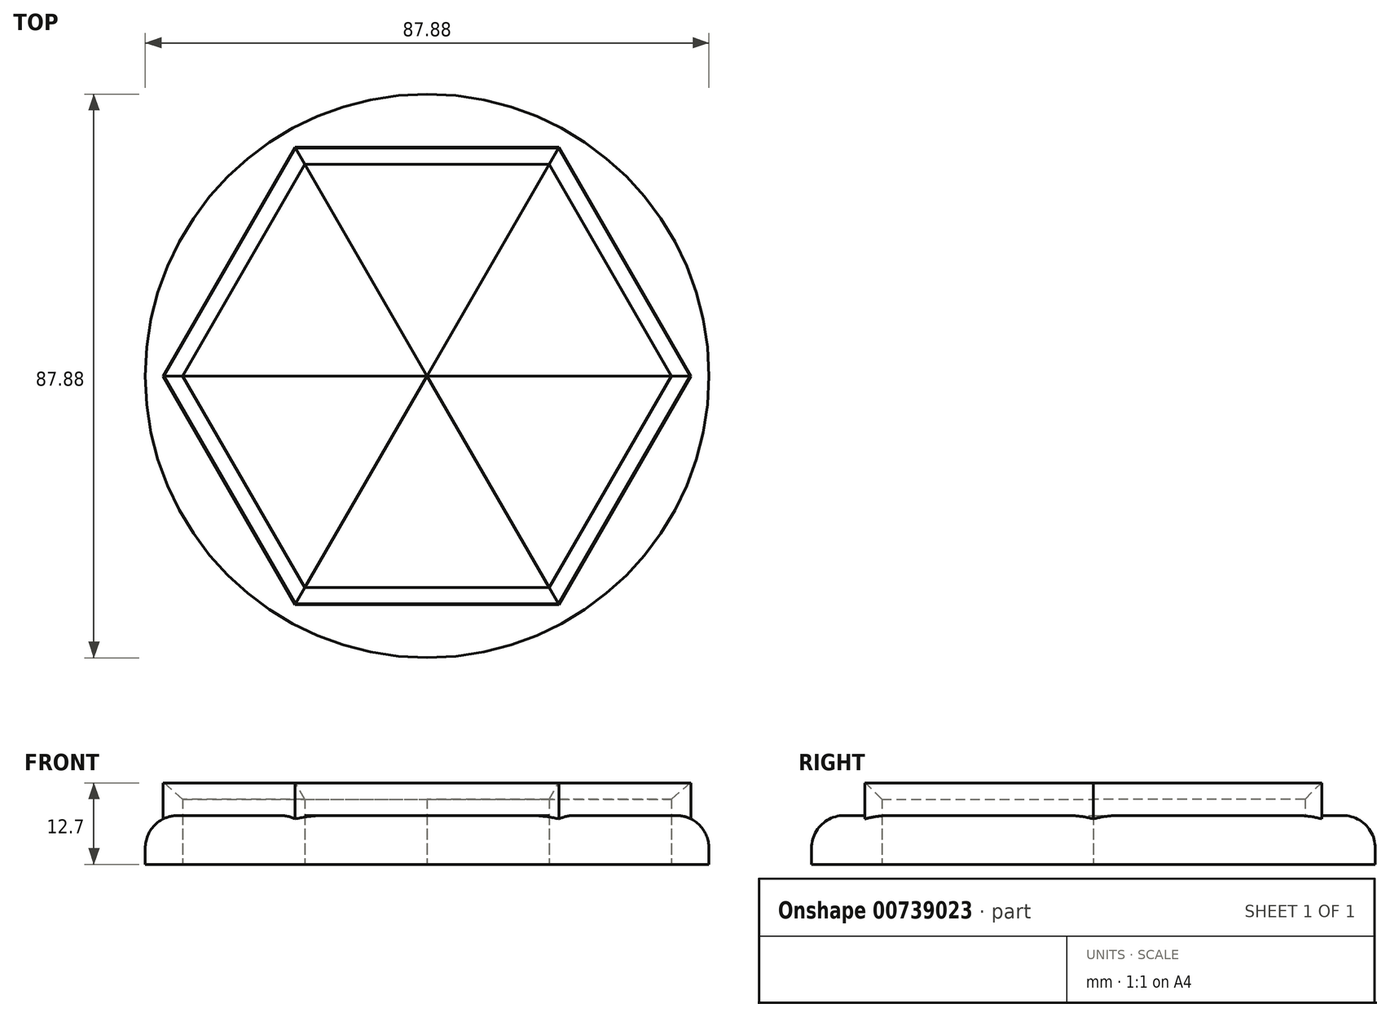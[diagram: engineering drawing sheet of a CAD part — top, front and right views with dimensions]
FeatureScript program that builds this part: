
annotation { "Feature Type Name" : "Feature", "Feature Type Description" : "" }
export const myFeature = defineFeature(function(context is Context, id is Id, definition is map)
    precondition{}
    {
        {
            var Q0;
            Q0=qCreatedBy(makeId("Top.planeOp"),FACE);
            var sketch = newSketch(context, id + "F0", { "sketchPlane" : qUnion([Q0])});
            skLineSegment(sketch, "E0.0", {"start": v(19.05, -33) * mm, "end": v(-19.05, -33) * mm});
            skLineSegment(sketch, "E0.1", {"start": v(-19.05, -33) * mm, "end": v(-38.1, 0) * mm});
            skLineSegment(sketch, "E0.2", {"start": v(-38.1, 0) * mm, "end": v(-19.05, 33) * mm});
            skLineSegment(sketch, "E0.3", {"start": v(-19.05, 33) * mm, "end": v(19.05, 33) * mm});
            skLineSegment(sketch, "E0.4", {"start": v(19.05, 33) * mm, "end": v(38.1, 0) * mm});
            skLineSegment(sketch, "E0.5", {"start": v(38.1, 0) * mm, "end": v(19.05, -33) * mm});
            skCircle(sketch, "E1", {"center": v(0, 0) * mm, "radius": 43.94 * mm});
            skLineSegment(sketch, "E2", {"start": v(-38.1, 0) * mm, "end": v(-43.94, 0) * mm});
            skLineSegment(sketch, "E3", {"start": v(-19.05, -33) * mm, "end": v(19.05, 33) * mm});
            skLineSegment(sketch, "E4", {"start": v(19.05, -33) * mm, "end": v(-19.05, 33) * mm});
            skLineSegment(sketch, "E5", {"start": v(-38.1, 0) * mm, "end": v(38.1, 0) * mm});
            skCircle(sketch, "E6", {"center": v(0, 0) * mm, "radius": 38.1 * mm, "construction": true});
            skCircle(sketch, "E7", {"center": v(0, 0) * mm, "radius": 41.15 * mm});
            skLineSegment(sketch, "E8", {"start": v(0, 38.1) * mm, "end": v(0, 41.15) * mm});
            skPoint(sketch, "E8.startSnap0", {"position": v(0, 33) * mm});
            skCircle(sketch, "E9.cCircle", {"center": v(0, 0) * mm, "radius": 41.15 * mm, "construction": true});
            skLineSegment(sketch, "E9.0", {"start": v(41.15, 0) * mm, "end": v(20.57, -35.64) * mm});
            skLineSegment(sketch, "E9.1", {"start": v(20.57, -35.64) * mm, "end": v(-20.57, -35.64) * mm});
            skLineSegment(sketch, "E9.2", {"start": v(-20.57, -35.64) * mm, "end": v(-41.15, 0) * mm});
            skLineSegment(sketch, "E9.3", {"start": v(-41.15, 0) * mm, "end": v(-20.57, 35.64) * mm});
            skLineSegment(sketch, "E9.4", {"start": v(-20.57, 35.64) * mm, "end": v(20.57, 35.64) * mm});
            skLineSegment(sketch, "E9.5", {"start": v(20.57, 35.64) * mm, "end": v(41.15, 0) * mm});
            skSolve(sketch);
        }
        {
            var Q0;
            Q0=makeQuery(id+"F0.imprint","IMPRINT",FACE,{"disambiguationData":[TD([[makeQuery(id+"F0.imprint","IMPRINT",EDGE,{"derivedFrom":sQuery(id+"F0.wireOp",EDGE,"E0.0")}),1.0]])]});
            extrude(context, id + "F1", {"entities" : qUnion([Q0]), "depth" : 12.7 * mm, "offsetDistance" : 25.4 * mm});
        }
        {
            var Q0;
            {var subQ0=sQuery(id+"F0.wireOp",EDGE,"E0.3");Q0=makeQuery(id+"F0.imprint","IMPRINT",FACE,{"disambiguationData":[TD([[makeQuery(id+"F0.imprint","IMPRINT",EDGE,{"derivedFrom":subQ0}),-1.0]])]});}
            extrude(context, id + "F2", {"entities" : qUnion([Q0]), "operationType" : NewBodyOperationType.ADD, "depth" : 10.16 * mm, "offsetDistance" : 25.4 * mm});
        }
        {
            var Q0;
            {var subQ0=sQuery(id+"F0.wireOp",EDGE,"E0.2");Q0=makeQuery(id+"F0.imprint","IMPRINT",FACE,{"disambiguationData":[TD([[makeQuery(id+"F0.imprint","IMPRINT",EDGE,{"derivedFrom":subQ0}),-1.0]])]});}
            extrude(context, id + "F3", {"entities" : qUnion([Q0]), "operationType" : NewBodyOperationType.ADD, "depth" : 7.62 * mm, "offsetDistance" : 25.4 * mm});
        }
        {
            var Q0;
            {var subQ0=sQuery(id+"F0.wireOp",EDGE,"E0.4");Q0=makeQuery(id+"F0.imprint","IMPRINT",FACE,{"disambiguationData":[TD([[makeQuery(id+"F0.imprint","IMPRINT",EDGE,{"derivedFrom":subQ0}),-1.0]])]});}
            extrude(context, id + "F4", {"entities" : qUnion([Q0]), "operationType" : NewBodyOperationType.ADD, "depth" : 7.62 * mm, "offsetDistance" : 25.4 * mm});
        }
        {
            var Q0;
            {var subQ0=sQuery(id+"F0.wireOp",EDGE,"E0.5");Q0=makeQuery(id+"F0.imprint","IMPRINT",FACE,{"disambiguationData":[TD([[makeQuery(id+"F0.imprint","IMPRINT",EDGE,{"derivedFrom":subQ0}),-1.0]])]});}
            extrude(context, id + "F5", {"entities" : qUnion([Q0]), "depth" : 10.16 * mm, "offsetDistance" : 25.4 * mm});
        }
        {
            var Q0;
            {var subQ0=sQuery(id+"F0.wireOp",EDGE,"E0.0");Q0=makeQuery(id+"F0.imprint","IMPRINT",FACE,{"disambiguationData":[TD([[makeQuery(id+"F0.imprint","IMPRINT",EDGE,{"derivedFrom":subQ0}),-1.0]])]});}
            extrude(context, id + "F6", {"entities" : qUnion([Q0]), "depth" : 7.62 * mm, "offsetDistance" : 25.4 * mm});
        }
        {
            var Q0;
            {var subQ0=sQuery(id+"F0.wireOp",EDGE,"E0.1");Q0=makeQuery(id+"F0.imprint","IMPRINT",FACE,{"disambiguationData":[TD([[makeQuery(id+"F0.imprint","IMPRINT",EDGE,{"derivedFrom":subQ0}),-1.0]])]});}
            extrude(context, id + "F7", {"entities" : qUnion([Q0]), "depth" : 10.16 * mm, "offsetDistance" : 25.4 * mm});
        }
        {
            var Q0;
            {var subQ0=sQuery(id+"F0.wireOp",EDGE,"E9.2");Q0=makeQuery(id+"F0.imprint","IMPRINT",FACE,{"disambiguationData":[TD([[makeQuery(id+"F0.imprint","IMPRINT",EDGE,{"derivedFrom":subQ0}),1.0]])]});}
            var Q1;
            {var subQ0=sQuery(id+"F0.wireOp",EDGE,"E9.1");Q1=makeQuery(id+"F0.imprint","IMPRINT",FACE,{"disambiguationData":[TD([[makeQuery(id+"F0.imprint","IMPRINT",EDGE,{"derivedFrom":subQ0}),1.0]])]});}
            var Q2;
            {var subQ0=sQuery(id+"F0.wireOp",EDGE,"E9.0");Q2=makeQuery(id+"F0.imprint","IMPRINT",FACE,{"disambiguationData":[TD([[makeQuery(id+"F0.imprint","IMPRINT",EDGE,{"derivedFrom":subQ0}),1.0]])]});}
            var Q3;
            Q3=makeQuery(id+"F0.imprint","IMPRINT",FACE,{"disambiguationData":[TD([[makeQuery(id+"F0.imprint","IMPRINT",EDGE,{"derivedFrom":sQuery(id+"F0.wireOp",EDGE,"E1")}),1.0]])]});
            var Q4;
            {var subQ0=sQuery(id+"F0.wireOp",EDGE,"E9.5");Q4=makeQuery(id+"F0.imprint","IMPRINT",FACE,{"disambiguationData":[TD([[makeQuery(id+"F0.imprint","IMPRINT",EDGE,{"derivedFrom":subQ0}),1.0]])]});}
            var Q5;
            {var subQ2=sQuery(id+"F0.wireOp",EDGE,"E9.4");Q5=makeQuery(id+"F0.imprint","IMPRINT",FACE,{"disambiguationData":[TD([[makeQuery(id+"F0.imprint","IMPRINT",EDGE,{"derivedFrom":subQ2}),1.0]])]});}
            var Q6;
            {var subQ0=sQuery(id+"F0.wireOp",EDGE,"E9.3");Q6=makeQuery(id+"F0.imprint","IMPRINT",FACE,{"disambiguationData":[TD([[makeQuery(id+"F0.imprint","IMPRINT",EDGE,{"derivedFrom":subQ0}),1.0]])]});}
            extrude(context, id + "F8", {"entities" : qUnion([Q0, Q1, Q2, Q3, Q4, Q5, Q6]), "operationType" : NewBodyOperationType.ADD, "depth" : 7.62 * mm, "offsetDistance" : 25.4 * mm});
        }
        {
            var Q0;
            Q0=makeQuery(id+"F8.opExtrude","CAP_EDGE",EDGE,{"disambiguationData":[OSD([sQuery(id+"F0.wireOp",EDGE,"E1")])],"isStart":false});
            fillet(context, id + "F9", {"entities" : qUnion([Q0]), "radius" : 5.08 * mm, "tangentPropagation" : true, "allowEdgeOverflow" : false});
        }
        {
            var Q0;
            Q0=makeQuery(id+"F1.opExtrude","CAP_EDGE",EDGE,{"disambiguationData":[OSD([sQuery(id+"F0.wireOp",EDGE,"E0.2")])],"isStart":false});
            var Q1;
            Q1=makeQuery(id+"F1.opExtrude","CAP_EDGE",EDGE,{"disambiguationData":[OSD([sQuery(id+"F0.wireOp",EDGE,"E0.5")])],"isStart":false});
            var Q2;
            Q2=makeQuery(id+"F1.opExtrude","CAP_EDGE",EDGE,{"disambiguationData":[OSD([sQuery(id+"F0.wireOp",EDGE,"E0.0")])],"isStart":false});
            var Q3;
            Q3=makeQuery(id+"F1.opExtrude","CAP_EDGE",EDGE,{"disambiguationData":[OSD([sQuery(id+"F0.wireOp",EDGE,"E0.1")])],"isStart":false});
            chamfer(context, id + "F10", {"entities" : qUnion([Q0, Q1, Q2, Q3]), "width" : 2.54 * mm, "tangentPropagation" : true});
        }
        {
            var Q0;
            Q0=makeQuery(id+"F1.opExtrude","CAP_EDGE",EDGE,{"disambiguationData":[OSD([sQuery(id+"F0.wireOp",EDGE,"E0.3")])],"isStart":false});
            chamfer(context, id + "F11", {"entities" : qUnion([Q0]), "width" : 2.54 * mm, "tangentPropagation" : true});
        }
        {
            var Q0;
            Q0=makeQuery(id+"F1.opExtrude","CAP_EDGE",EDGE,{"disambiguationData":[OSD([sQuery(id+"F0.wireOp",EDGE,"E0.4")])],"isStart":false});
            chamfer(context, id + "F12", {"entities" : qUnion([Q0]), "width" : 2.54 * mm, "tangentPropagation" : true});
        }
    });
